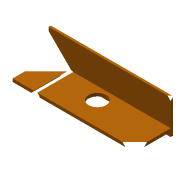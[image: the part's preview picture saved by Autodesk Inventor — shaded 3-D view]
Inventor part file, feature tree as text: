
AUTODESK INVENTOR PART (.ipt)
format: ipt  version: 2016 (Build 200138000, 138)  size: 156,672 bytes
history: native  units: in
note: dims shown in document units (in); Inventor stores cm internally (conversion verified against a paired STEP export)
features: reference x10, sketch x7, extrude x4, hole x3, other x1, plane x1, chamfer x1
ambient origin geometry x8: Origin, YZ Plane, XZ Plane, XY Plane, X Axis, Y Axis, Z Axis, Center Point
bodies: Solid1 (feature_tree)
feature tree (27):
  other  "skeleton.ipt"
  extrude  "Extrusion1"  Depth=0.3937in
  plane  "Work Plane1"
  extrude  "Extrusion3"  Depth=0.1181in TaperAngle=0.0deg
  hole  "Hole1"  [1 undecoded]
  hole  "Hole2"  [1 undecoded]
  extrude  "Extrusion4"  Depth=0.1575in
  extrude  "Extrusion5"  Depth=0.1575in
  hole  "Hole3"  [1 undecoded]
  chamfer  "Chamfer1"  Distance=5.9055in
  sketch  "Sketch1"  dims[d0=0.3937in d1=5.9055in]
  sketch  "Sketch3"  dims[d2=2.9528in d3=0.1181in d4=0.0in]
  sketch  "Sketch4"  dims[d9=0.0394in d10=5.9055in]
  sketch  "Sketch5"  dims[d11=1.9685in d12=0.1575in d13=0.0in]
  sketch  "Sketch6"  dims[d14=3.5433in]
  sketch  "Sketch8"  dims[d15=0.9055in d16=0.2362in d17=0.1575in d18=0.0787in d19=90.0deg d20=0.315in d21=0.8108in d22=1.1811in]
  sketch  "Sketch9"  dims[d23=0.4331in d24=0.2362in d25=0.1575in d26=0.0787in d27=90.0deg d28=0.315in d29=0.8108in d31=1.4764in d32=0.0in d33=5.9055in d34=0.1181in d35=0.0in d37=0.0394in d38=1.9685in d39=0.1181in d40=0.0in d41=0.1024in d42=0.2362in d43=0.1575in d44=0.0787in d45=90.0deg d46=0.315in d47=0.8108in d48=0.0394in d49=0.0787in d50=45.0deg]
  reference  "Reference1"
  reference  "Reference2"
  reference  "Reference3"
  reference  "Reference4"
  reference  "Reference5"
  reference  "Reference6"
  reference  "Reference7"
  reference  "Reference8"
  reference  "Reference9"
  reference  "Reference10"
note: 3 required parameter values undecoded (feature->parameter linkage not recoverable at this tier; creation-order binding heuristic only, values carry confidence <= 0.55)
